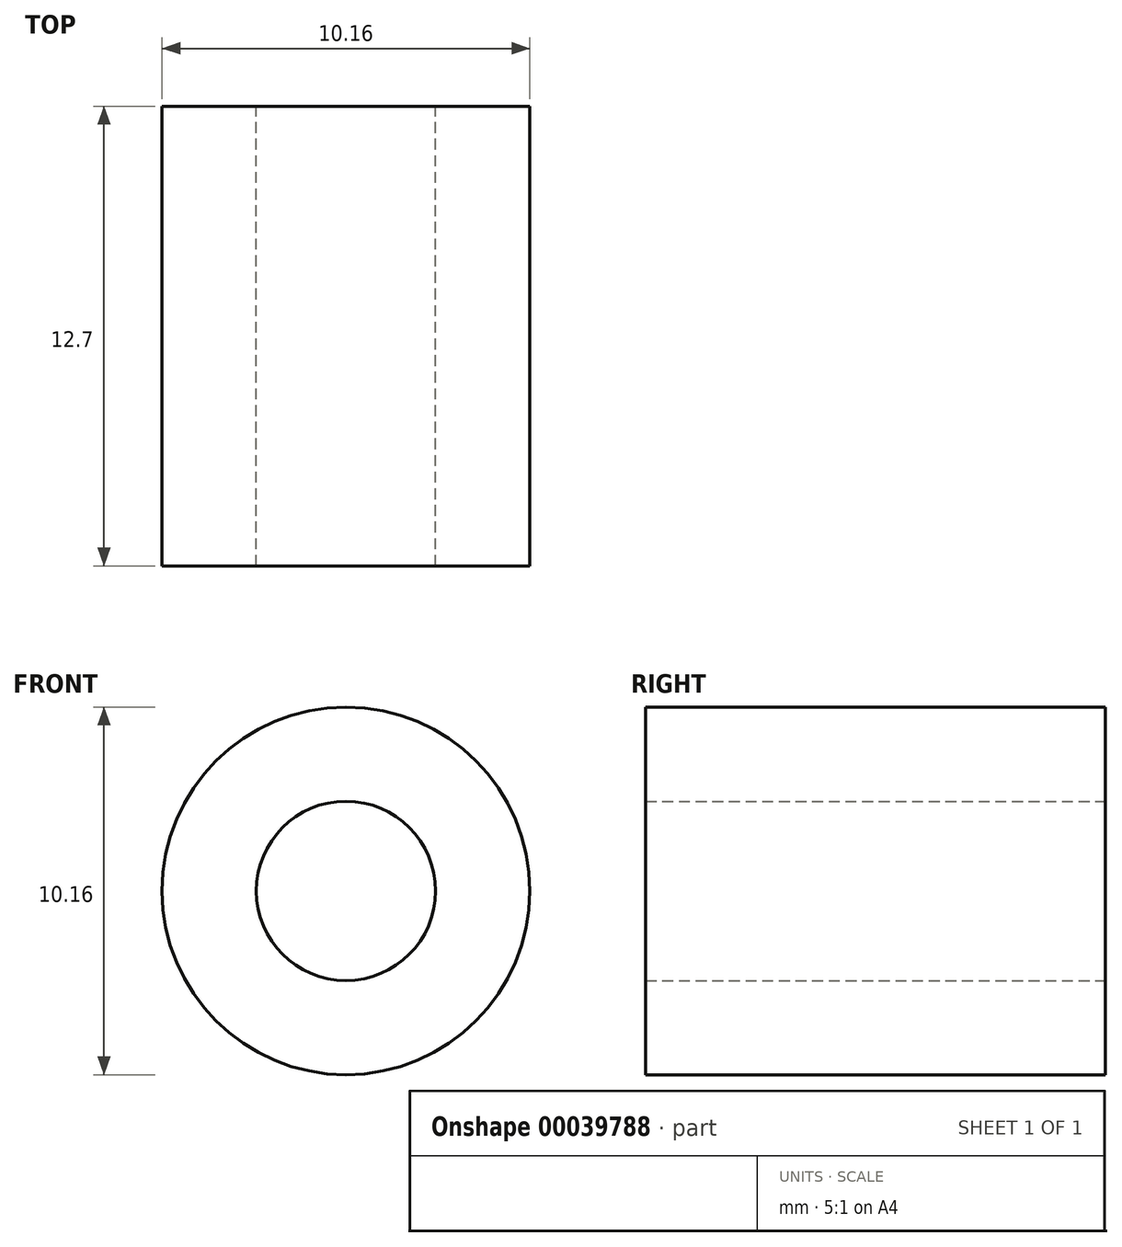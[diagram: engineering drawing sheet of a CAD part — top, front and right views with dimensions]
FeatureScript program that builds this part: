
annotation { "Feature Type Name" : "Feature", "Feature Type Description" : "" }
export const myFeature = defineFeature(function(context is Context, id is Id, definition is map)
    precondition{}
    {
        {
            var Q0;
            Q0=qCreatedBy(makeId("Front.planeOp"),FACE);
            var sketch = newSketch(context, id + "F0", { "sketchPlane" : qUnion([Q0])});
            skLineSegment(sketch, "E0", {"start": v(0, 0) * mm, "end": v(2.48, 0) * mm, "construction": true});
            skLineSegment(sketch, "E1", {"start": v(0, 0) * mm, "end": v(5.08, 0) * mm, "construction": true});
            skCircle(sketch, "E2", {"center": v(0, 0) * mm, "radius": 5.08 * mm});
            skPoint(sketch, "E3.0.midPoint", {"position": v(2.48, 0) * mm});
            skCircle(sketch, "E4", {"center": v(0, 0) * mm, "radius": 2.48 * mm});
            skLineSegment(sketch, "E5", {"start": v(-3.02, 4.09) * mm, "end": v(3.02, 4.09) * mm, "construction": true});
            skLineSegment(sketch, "E6", {"start": v(3.02, 4.09) * mm, "end": v(3.02, -4.09) * mm, "construction": true});
            skLineSegment(sketch, "E7", {"start": v(3.02, -4.09) * mm, "end": v(-3.02, -4.09) * mm, "construction": true});
            skLineSegment(sketch, "E8", {"start": v(-3.02, -4.09) * mm, "end": v(-3.02, 4.09) * mm, "construction": true});
            skLineSegment(sketch, "E9", {"start": v(-5.08, 0) * mm, "end": v(5.08, 0) * mm, "construction": true});
            skLineSegment(sketch, "E10", {"start": v(0, 5.08) * mm, "end": v(0, -5.08) * mm, "construction": true});
            skSolve(sketch);
        }
        {
            var Q0;
            Q0 = qSketchRegion(id + "F0", true);
            extrude(context, id + "F1", {"entities" : qUnion([Q0]), "depth" : 12.7 * mm});
        }
    });
